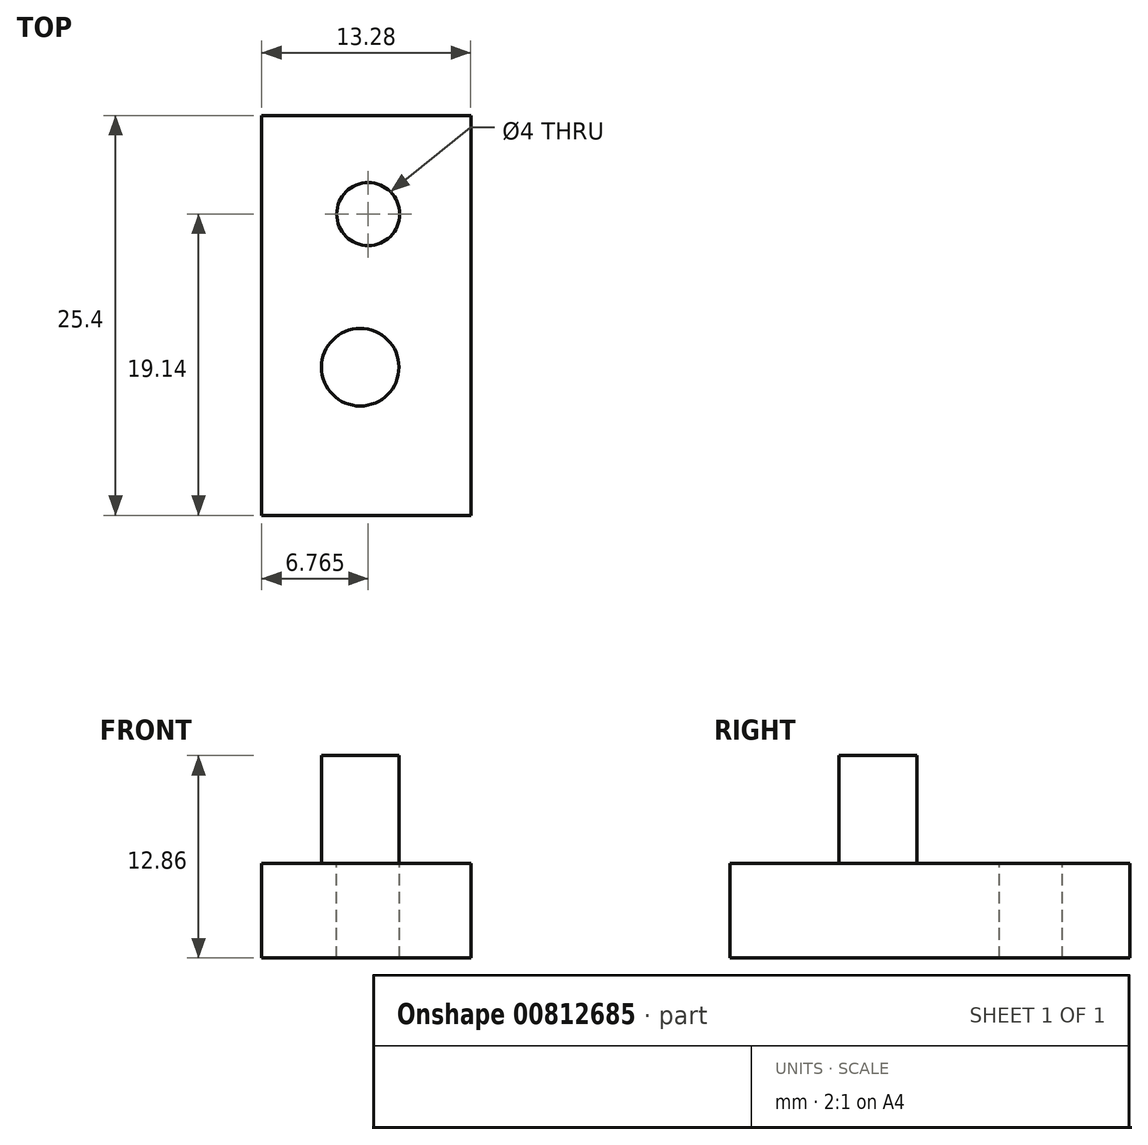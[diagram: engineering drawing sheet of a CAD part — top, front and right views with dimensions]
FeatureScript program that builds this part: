
annotation { "Feature Type Name" : "Feature", "Feature Type Description" : "" }
export const myFeature = defineFeature(function(context is Context, id is Id, definition is map)
    precondition{}
    {
        {
            var Q0;
            Q0=qCreatedBy(makeId("Front.planeOp"),FACE);
            var sketch = newSketch(context, id + "F0", { "sketchPlane" : qUnion([Q0])});
            skLineSegment(sketch, "E0.bottom", {"start": v(-32.78, 30.75) * mm, "end": v(-19.5, 30.75) * mm});
            skLineSegment(sketch, "E0.top", {"start": v(-32.78, 24.75) * mm, "end": v(-19.5, 24.75) * mm});
            skLineSegment(sketch, "E0.left", {"start": v(-32.78, 30.75) * mm, "end": v(-32.78, 24.75) * mm});
            skLineSegment(sketch, "E0.right", {"start": v(-19.5, 30.75) * mm, "end": v(-19.5, 24.75) * mm});
            skSolve(sketch);
        }
        {
            var Q0;
            Q0=makeQuery(id+"F0.imprint","IMPRINT",FACE,{"disambiguationData":[TD([[makeQuery(id+"F0.imprint","IMPRINT",EDGE,{"derivedFrom":sQuery(id+"F0.wireOp",EDGE,"E0.bottom")}),-1.0]])]});
            extrude(context, id + "F1", {"entities" : qUnion([Q0]), "depth" : 25.4 * mm, "offsetDistance" : 25.4 * mm});
        }
        {
            var Q0;
            Q0=makeQuery(id+"F1.opExtrude","SWEPT_FACE",FACE,{"disambiguationData":[OSD([sQuery(id+"F0.wireOp",EDGE,"E0.bottom")])]});
            var sketch = newSketch(context, id + "F2", { "sketchPlane" : qUnion([Q0])});
            skCircle(sketch, "E1", {"center": v(-26.01, -6.26) * mm, "radius": 2 * mm});
            skSolve(sketch);
        }
        {
            var Q0;
            Q0 = qSketchRegion(id + "F2", true);
            extrude(context, id + "F3", {"entities" : qUnion([Q0]), "operationType" : NewBodyOperationType.REMOVE, "oppositeDirection" : true, "depth" : 25.4 * mm, "offsetDistance" : 25.4 * mm});
        }
        {
            var Q0;
            Q0=makeQuery(id+"F1.opExtrude","SWEPT_FACE",FACE,{"disambiguationData":[OSD([sQuery(id+"F0.wireOp",EDGE,"E0.bottom")])]});
            var sketch = newSketch(context, id + "F4", { "sketchPlane" : qUnion([Q0])});
            skCircle(sketch, "E2", {"center": v(-26.52, -15.99) * mm, "radius": 2.46 * mm});
            skSolve(sketch);
        }
        {
            var Q0;
            Q0=makeQuery(id+"F4.imprint","IMPRINT",FACE,{"disambiguationData":[TD([[makeQuery(id+"F4.imprint","IMPRINT",EDGE,{"derivedFrom":sQuery(id+"F4.wireOp",EDGE,"E2")}),1.0]])]});
            extrude(context, id + "F5", {"entities" : qUnion([Q0]), "operationType" : NewBodyOperationType.ADD, "depth" : 6.86 * mm, "offsetDistance" : 25.4 * mm});
        }
    });
